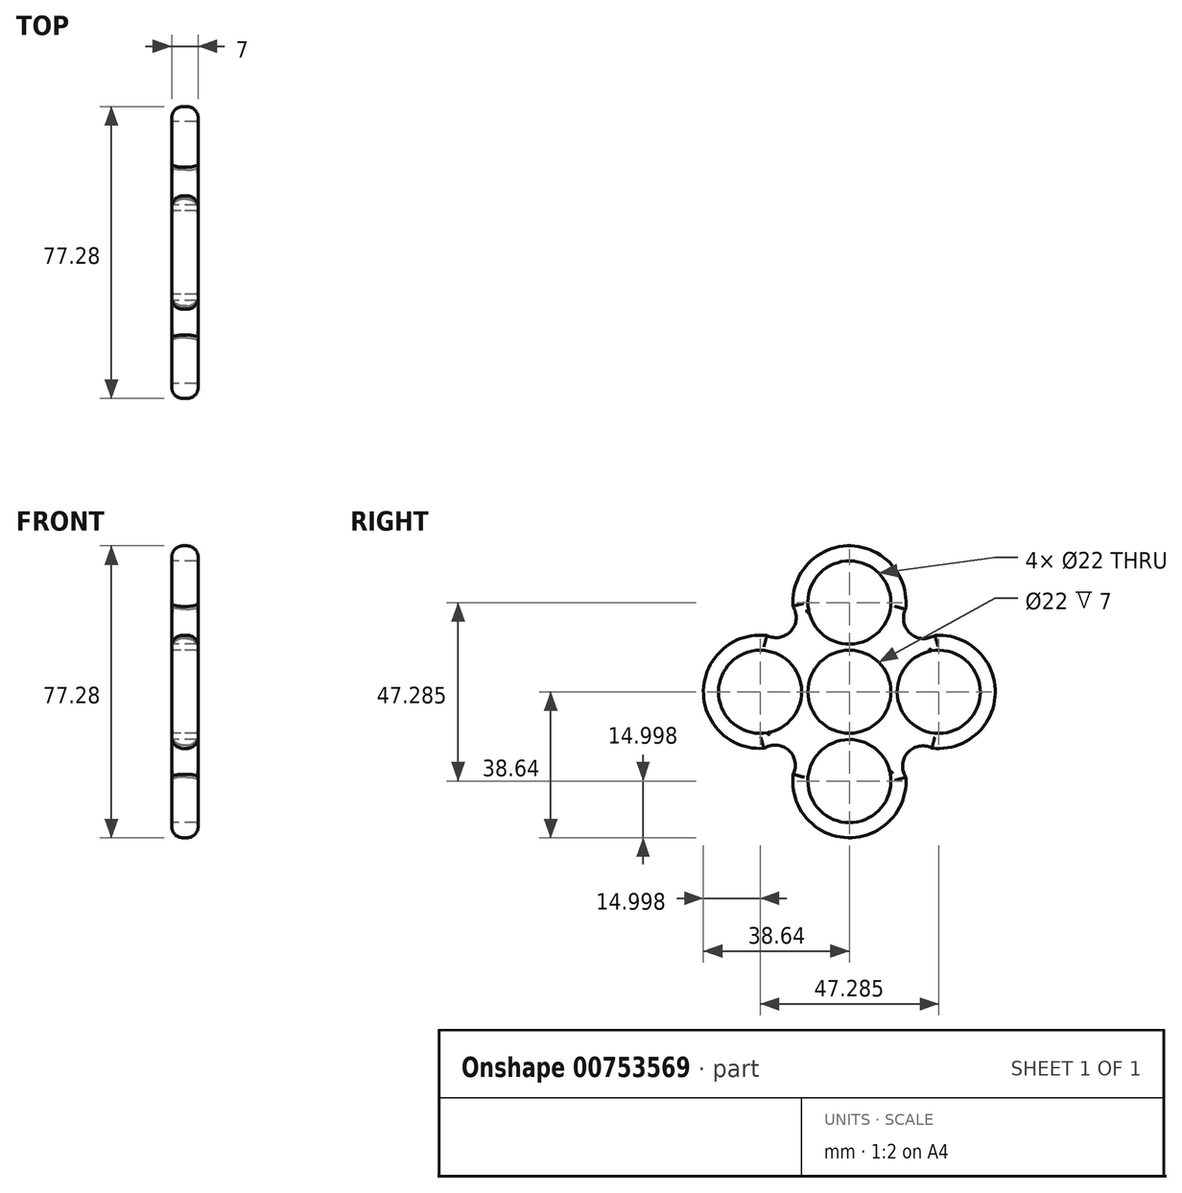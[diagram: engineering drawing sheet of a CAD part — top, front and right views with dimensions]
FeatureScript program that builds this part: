
annotation { "Feature Type Name" : "Feature", "Feature Type Description" : "" }
export const myFeature = defineFeature(function(context is Context, id is Id, definition is map)
    precondition{}
    {
        {
            var Q0;
            Q0=qCreatedBy(makeId("Right.planeOp"),FACE);
            var sketch = newSketch(context, id + "F0", { "sketchPlane" : qUnion([Q0])});
            skPoint(sketch, "E0.center", {"position": v(0, 0) * mm});
            skCircle(sketch, "E1", {"center": v(0, 23.64) * mm, "radius": 15 * mm});
            skCircle(sketch, "E2.1.0", {"center": v(-23.64, 0) * mm, "radius": 15 * mm});
            skCircle(sketch, "E2.2.0", {"center": v(0, -23.64) * mm, "radius": 15 * mm});
            skCircle(sketch, "E2.3.0", {"center": v(23.64, 0) * mm, "radius": 15 * mm});
            skArc(sketch, "E3", {"start": v(14.9, 21.83) * mm, "mid": v(16.1, 15.45) * mm, "end": v(22.6, 14.96) * mm});
            skArc(sketch, "E4.1.0", {"start": v(-21.83, 14.9) * mm, "mid": v(-15.45, 16.1) * mm, "end": v(-14.96, 22.6) * mm});
            skArc(sketch, "E4.2.0", {"start": v(-14.9, -21.83) * mm, "mid": v(-16.1, -15.45) * mm, "end": v(-22.6, -14.96) * mm});
            skArc(sketch, "E4.3.0", {"start": v(21.83, -14.9) * mm, "mid": v(15.45, -16.1) * mm, "end": v(14.96, -22.6) * mm});
            skCircle(sketch, "E5", {"center": v(0, -23.64) * mm, "radius": 11 * mm});
            skCircle(sketch, "E6.1.0", {"center": v(23.64, 0) * mm, "radius": 11 * mm});
            skCircle(sketch, "E6.2.0", {"center": v(0, 23.64) * mm, "radius": 11 * mm});
            skCircle(sketch, "E6.3.0", {"center": v(-23.64, 0) * mm, "radius": 11 * mm});
            skSolve(sketch);
        }
        {
            var Q0;
            {var subQ0=sQuery(id+"F0.wireOp",EDGE,"E4.2.0");var subQ1=sQuery(id+"F0.wireOp",EDGE,"E2.1.0");var subQ2=makeQuery(id+"F0.imprint","INTERSECT",VERTEX,{"disambiguationData":[OD(1.0)],"derivedFrom":[subQ1,subQ0]});Q0=makeQuery(id+"F0.imprint","IMPRINT",FACE,{"disambiguationData":[TD([[makeQuery(id+"F0.imprint","IMPRINT",EDGE,{"disambiguationData":[TD([[subQ2,-1.0]])],"derivedFrom":subQ1}),1.0]])]});}
            var Q1;
            {var subQ0=sQuery(id+"F0.wireOp",EDGE,"E4.1.0");var subQ1=sQuery(id+"F0.wireOp",EDGE,"E1");var subQ2=makeQuery(id+"F0.imprint","INTERSECT",VERTEX,{"disambiguationData":[OD(1.0)],"derivedFrom":[subQ1,subQ0]});Q1=makeQuery(id+"F0.imprint","IMPRINT",FACE,{"disambiguationData":[TD([[makeQuery(id+"F0.imprint","IMPRINT",EDGE,{"disambiguationData":[TD([[subQ2,-1.0]])],"derivedFrom":subQ1}),1.0]])]});}
            var Q2;
            {var subQ9=sQuery(id+"F0.wireOp",EDGE,"E4.1.0");var subQ10=sQuery(id+"F0.wireOp",EDGE,"E1");var subQ11=makeQuery(id+"F0.imprint","INTERSECT",VERTEX,{"disambiguationData":[OD(1.0)],"derivedFrom":[subQ10,subQ9]});Q2=makeQuery(id+"F0.imprint","IMPRINT",FACE,{"disambiguationData":[TD([[makeQuery(id+"F0.imprint","IMPRINT",EDGE,{"disambiguationData":[TD([[subQ11,-1.0]])],"derivedFrom":subQ10}),-1.0]])]});}
            var Q3;
            {var subQ0=sQuery(id+"F0.wireOp",EDGE,"E3");var subQ1=sQuery(id+"F0.wireOp",EDGE,"E2.3.0");var subQ2=makeQuery(id+"F0.imprint","INTERSECT",VERTEX,{"disambiguationData":[OD(1.0)],"derivedFrom":[subQ1,subQ0]});Q3=makeQuery(id+"F0.imprint","IMPRINT",FACE,{"disambiguationData":[TD([[makeQuery(id+"F0.imprint","IMPRINT",EDGE,{"disambiguationData":[TD([[subQ2,-1.0]])],"derivedFrom":subQ1}),1.0]])]});}
            var Q4;
            {var subQ0=sQuery(id+"F0.wireOp",EDGE,"E4.3.0");var subQ1=sQuery(id+"F0.wireOp",EDGE,"E2.2.0");var subQ2=makeQuery(id+"F0.imprint","INTERSECT",VERTEX,{"disambiguationData":[OD(1.0)],"derivedFrom":[subQ1,subQ0]});Q4=makeQuery(id+"F0.imprint","IMPRINT",FACE,{"disambiguationData":[TD([[makeQuery(id+"F0.imprint","IMPRINT",EDGE,{"disambiguationData":[TD([[subQ2,-1.0]])],"derivedFrom":subQ1}),1.0]])]});}
            extrude(context, id + "F1", {"entities" : qUnion([Q0, Q1, Q2, Q3, Q4]), "depth" : 7 * mm, "offsetDistance" : 25.4 * mm});
        }
        {
            var Q0;
            Q0=makeQuery(id+"F1.opExtrude","CAP_EDGE",EDGE,{"disambiguationData":[OSD([sQuery(id+"F0.wireOp",EDGE,"E1")])],"isStart":false});
            var Q1;
            Q1=makeQuery(id+"F1.opExtrude","CAP_EDGE",EDGE,{"disambiguationData":[OSD([sQuery(id+"F0.wireOp",EDGE,"E4.1.0")])],"isStart":false});
            var Q2;
            Q2=makeQuery(id+"F1.opExtrude","CAP_EDGE",EDGE,{"disambiguationData":[OSD([sQuery(id+"F0.wireOp",EDGE,"E2.1.0")])],"isStart":false});
            var Q3;
            Q3=makeQuery(id+"F1.opExtrude","CAP_EDGE",EDGE,{"disambiguationData":[OSD([sQuery(id+"F0.wireOp",EDGE,"E4.2.0")])],"isStart":false});
            var Q4;
            Q4=makeQuery(id+"F1.opExtrude","CAP_EDGE",EDGE,{"disambiguationData":[OSD([sQuery(id+"F0.wireOp",EDGE,"E2.2.0")])],"isStart":false});
            var Q5;
            Q5=makeQuery(id+"F1.opExtrude","CAP_EDGE",EDGE,{"disambiguationData":[OSD([sQuery(id+"F0.wireOp",EDGE,"E3")])],"isStart":false});
            var Q6;
            Q6=makeQuery(id+"F1.opExtrude","CAP_EDGE",EDGE,{"disambiguationData":[OSD([sQuery(id+"F0.wireOp",EDGE,"E2.3.0")])],"isStart":false});
            var Q7;
            Q7=makeQuery(id+"F1.opExtrude","CAP_EDGE",EDGE,{"disambiguationData":[OSD([sQuery(id+"F0.wireOp",EDGE,"E4.3.0")])],"isStart":false});
            var Q8;
            Q8=makeQuery(id+"F1.opExtrude","CAP_EDGE",EDGE,{"disambiguationData":[OSD([sQuery(id+"F0.wireOp",EDGE,"E2.1.0")])],"isStart":true});
            var Q9;
            Q9=makeQuery(id+"F1.opExtrude","CAP_EDGE",EDGE,{"disambiguationData":[OSD([sQuery(id+"F0.wireOp",EDGE,"E4.2.0")])],"isStart":true});
            var Q10;
            Q10=makeQuery(id+"F1.opExtrude","CAP_EDGE",EDGE,{"disambiguationData":[OSD([sQuery(id+"F0.wireOp",EDGE,"E2.2.0")])],"isStart":true});
            var Q11;
            Q11=makeQuery(id+"F1.opExtrude","CAP_EDGE",EDGE,{"disambiguationData":[OSD([sQuery(id+"F0.wireOp",EDGE,"E4.3.0")])],"isStart":true});
            var Q12;
            Q12=makeQuery(id+"F1.opExtrude","CAP_EDGE",EDGE,{"disambiguationData":[OSD([sQuery(id+"F0.wireOp",EDGE,"E2.3.0")])],"isStart":true});
            var Q13;
            Q13=makeQuery(id+"F1.opExtrude","CAP_EDGE",EDGE,{"disambiguationData":[OSD([sQuery(id+"F0.wireOp",EDGE,"E3")])],"isStart":true});
            var Q14;
            Q14=makeQuery(id+"F1.opExtrude","CAP_EDGE",EDGE,{"disambiguationData":[OSD([sQuery(id+"F0.wireOp",EDGE,"E1")])],"isStart":true});
            var Q15;
            Q15=makeQuery(id+"F1.opExtrude","CAP_EDGE",EDGE,{"disambiguationData":[OSD([sQuery(id+"F0.wireOp",EDGE,"E4.1.0")])],"isStart":true});
            fillet(context, id + "F2", {"entities" : qUnion([Q0, Q1, Q2, Q3, Q4, Q5, Q6, Q7, Q8, Q9, Q10, Q11, Q12, Q13, Q14, Q15]), "radius" : 3 * mm, "tangentPropagation" : true, "allowEdgeOverflow" : false});
        }
        {
            var Q0;
            Q0=qCreatedBy(makeId("Right.planeOp"),FACE);
            var sketch = newSketch(context, id + "F3", { "sketchPlane" : qUnion([Q0])});
            skCircle(sketch, "E7", {"center": v(0, 0) * mm, "radius": 11 * mm});
            skSolve(sketch);
        }
        {
            var Q0;
            Q0=makeQuery(id+"F3.imprint","IMPRINT",FACE,{"disambiguationData":[TD([[makeQuery(id+"F3.imprint","IMPRINT",EDGE,{"derivedFrom":sQuery(id+"F3.wireOp",EDGE,"E7")}),1.0]])]});
            extrude(context, id + "F4", {"entities" : qUnion([Q0]), "operationType" : NewBodyOperationType.REMOVE, "oppositeDirection" : true, "depth" : -7 * mm, "offsetDistance" : 25.4 * mm});
        }
        {
            var Q0;
            Q0=makeQuery(id+"F1.opExtrude","CAP_EDGE",EDGE,{"disambiguationData":[OSD([sQuery(id+"F0.wireOp",EDGE,"E6.1.0")])],"isStart":true});
            var Q1;
            Q1=makeQuery(id+"F1.opExtrude","CAP_EDGE",EDGE,{"disambiguationData":[OSD([sQuery(id+"F0.wireOp",EDGE,"E6.2.0")])],"isStart":true});
            var Q2;
            Q2=makeQuery(id+"F4.boolean.opBoolean","COPY",EDGE,{"derivedFrom":makeQuery(id+"F4.opExtrude","CAP_EDGE",EDGE,{"disambiguationData":[OSD([sQuery(id+"F3.wireOp",EDGE,"E7")])],"isStart":true})});
            var Q3;
            Q3=makeQuery(id+"F1.opExtrude","CAP_EDGE",EDGE,{"disambiguationData":[OSD([sQuery(id+"F0.wireOp",EDGE,"E6.3.0")])],"isStart":true});
            var Q4;
            Q4=makeQuery(id+"F1.opExtrude","CAP_EDGE",EDGE,{"disambiguationData":[OSD([sQuery(id+"F0.wireOp",EDGE,"E5")])],"isStart":true});
            var Q5;
            Q5=makeQuery(id+"F1.opExtrude","CAP_EDGE",EDGE,{"disambiguationData":[OSD([sQuery(id+"F0.wireOp",EDGE,"E6.1.0")])],"isStart":false});
            var Q6;
            Q6=makeQuery(id+"F1.opExtrude","CAP_EDGE",EDGE,{"disambiguationData":[OSD([sQuery(id+"F0.wireOp",EDGE,"E6.2.0")])],"isStart":false});
            var Q7;
            Q7=makeQuery(id+"F4.boolean.opBoolean","COPY",EDGE,{"derivedFrom":makeQuery(id+"F4.opExtrude","CAP_EDGE",EDGE,{"disambiguationData":[OSD([sQuery(id+"F3.wireOp",EDGE,"E7")])],"isStart":false})});
            var Q8;
            Q8=makeQuery(id+"F1.opExtrude","CAP_EDGE",EDGE,{"disambiguationData":[OSD([sQuery(id+"F0.wireOp",EDGE,"E5")])],"isStart":false});
            var Q9;
            Q9=makeQuery(id+"F1.opExtrude","CAP_EDGE",EDGE,{"disambiguationData":[OSD([sQuery(id+"F0.wireOp",EDGE,"E6.3.0")])],"isStart":false});
            fillet(context, id + "F5", {"entities" : qUnion([Q0, Q1, Q2, Q3, Q4, Q5, Q6, Q7, Q8, Q9]), "radius" : .5 * mm, "tangentPropagation" : true, "allowEdgeOverflow" : false});
        }
    });
